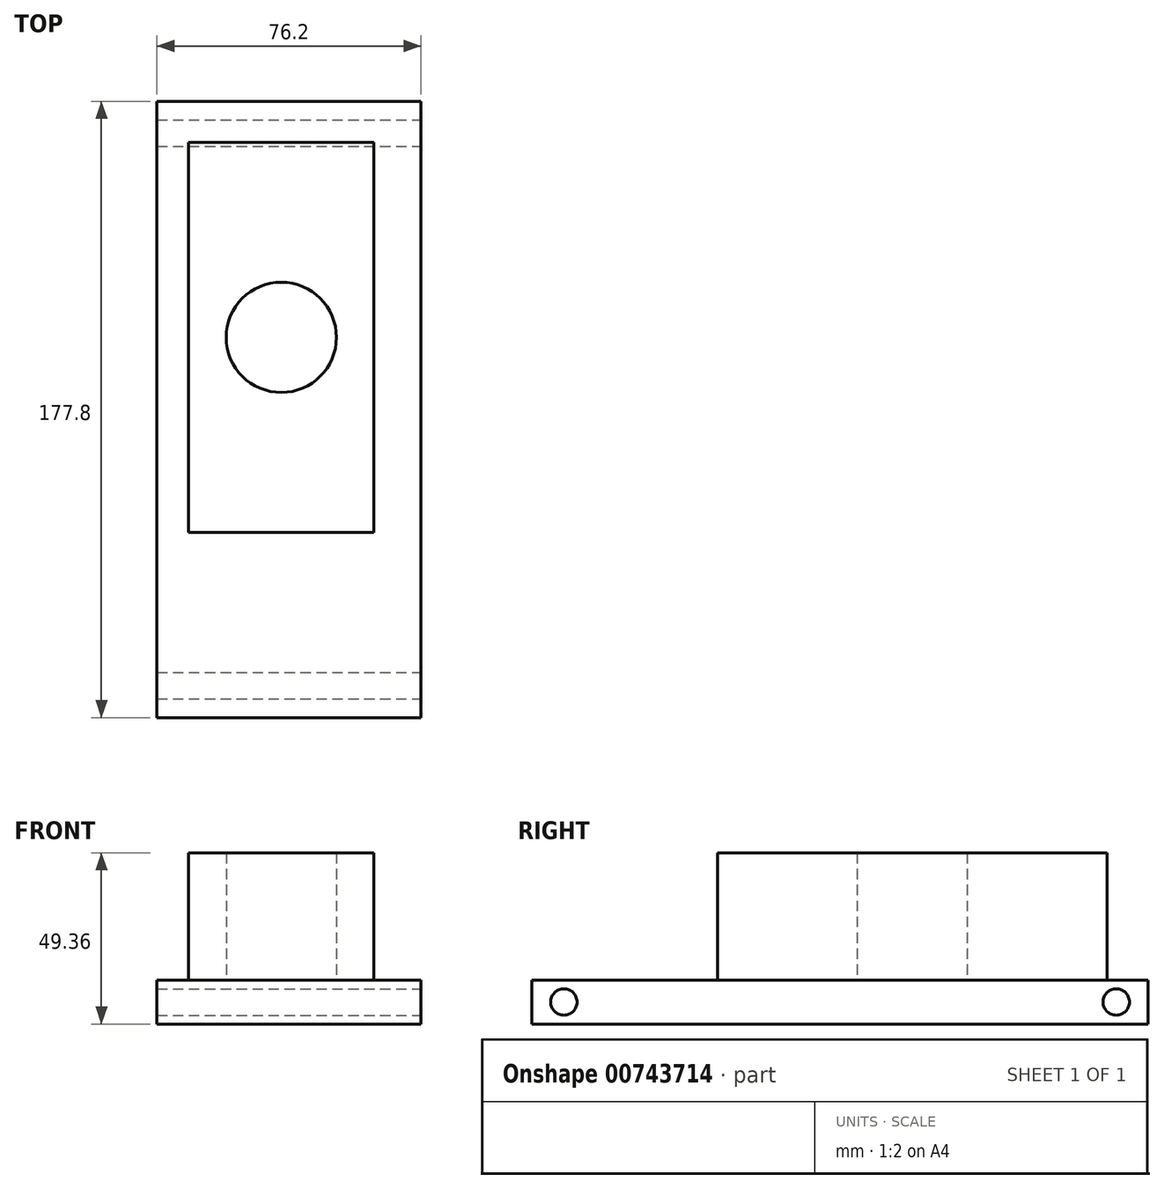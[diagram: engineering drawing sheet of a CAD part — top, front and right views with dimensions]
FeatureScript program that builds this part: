
annotation { "Feature Type Name" : "Feature", "Feature Type Description" : "" }
export const myFeature = defineFeature(function(context is Context, id is Id, definition is map)
    precondition{}
    {
        {
            var Q0;
            Q0=qCreatedBy(makeId("Top.planeOp"),FACE);
            var sketch = newSketch(context, id + "F0", { "sketchPlane" : qUnion([Q0])});
            skLineSegment(sketch, "E0.bottom", {"start": v(-49.4, 89.52) * mm, "end": v(26.8, 89.52) * mm});
            skLineSegment(sketch, "E0.top", {"start": v(-49.4, -88.28) * mm, "end": v(26.8, -88.28) * mm});
            skLineSegment(sketch, "E0.left", {"start": v(-49.4, 89.52) * mm, "end": v(-49.4, -88.28) * mm});
            skLineSegment(sketch, "E0.right", {"start": v(26.8, 89.52) * mm, "end": v(26.8, -88.28) * mm});
            skSolve(sketch);
        }
        {
            var Q0;
            Q0=makeQuery(id+"F0.imprint","IMPRINT",FACE,{"disambiguationData":[TD([[makeQuery(id+"F0.imprint","IMPRINT",EDGE,{"derivedFrom":sQuery(id+"F0.wireOp",EDGE,"E0.bottom")}),-1.0]])]});
            extrude(context, id + "F1", {"entities" : qUnion([Q0]), "depth" : 12.7 * mm, "offsetDistance" : 25.4 * mm});
        }
        {
            var Q0;
            Q0=makeQuery(id+"F1.opExtrude","SWEPT_FACE",FACE,{"disambiguationData":[OSD([sQuery(id+"F0.wireOp",EDGE,"E0.right")])]});
            var sketch = newSketch(context, id + "F2", { "sketchPlane" : qUnion([Q0])});
            skCircle(sketch, "E1", {"center": v(-79.06, 6.35) * mm, "radius": 3.81 * mm});
            skPoint(sketch, "E1.centerSnap0", {"position": v(-88.28, 6.35) * mm});
            skLineSegment(sketch, "E2", {"start": v(0.62, 12.7) * mm, "end": v(0.62, 0) * mm});
            skCircle(sketch, "E3.MirrorC", {"center": v(80.3, 6.35) * mm, "radius": 3.81 * mm});
            skSolve(sketch);
        }
        {
            var Q0;
            Q0=sQuery(id+"F2.wireOp",VERTEX,"E1.center");
            var Q1;
            Q1=makeQuery(id+"F1.opExtrude","SWEPT_BODY",BODY,{"disambiguationData":[OSD([sQuery(id+"F0.wireOp",EDGE,"E0.bottom"),sQuery(id+"F0.wireOp",EDGE,"E0.top"),sQuery(id+"F0.wireOp",EDGE,"E0.left"),sQuery(id+"F0.wireOp",EDGE,"E0.right")])]});
            hole(context, id + "F3", {"style" : HoleStyle.SIMPLE, "endStyle" : HoleEndStyle.THROUGH, "holeDiameter" : 7.62 * mm, "majorDiameter" : 6.35 * mm, "isTappedThrough" : true, "tappedDepth" : 12.7 * mm, "tapClearance" : 3, "locations" : qUnion([Q0]), "scope" : qUnion([Q1])});
        }
        {
            var Q0;
            Q0=sQuery(id+"F2.wireOp",VERTEX,"E3.MirrorC.center");
            var Q1;
            Q1=makeQuery(id+"F1.opExtrude","SWEPT_BODY",BODY,{"disambiguationData":[OSD([sQuery(id+"F0.wireOp",EDGE,"E0.bottom"),sQuery(id+"F0.wireOp",EDGE,"E0.top"),sQuery(id+"F0.wireOp",EDGE,"E0.left"),sQuery(id+"F0.wireOp",EDGE,"E0.right")])]});
            hole(context, id + "F4", {"style" : HoleStyle.SIMPLE, "endStyle" : HoleEndStyle.THROUGH, "holeDiameter" : 7.62 * mm, "majorDiameter" : 6.35 * mm, "isTappedThrough" : true, "tappedDepth" : 12.7 * mm, "tapClearance" : 3, "locations" : qUnion([Q0]), "scope" : qUnion([Q1])});
        }
        {
            var Q0;
            Q0=makeQuery(id+"F1.opExtrude","CAP_FACE",FACE,{"disambiguationData":[OSD([sQuery(id+"F0.wireOp",EDGE,"E0.bottom"),sQuery(id+"F0.wireOp",EDGE,"E0.top"),sQuery(id+"F0.wireOp",EDGE,"E0.left"),sQuery(id+"F0.wireOp",EDGE,"E0.right")])],"isStart":false});
            var sketch = newSketch(context, id + "F5", { "sketchPlane" : qUnion([Q0])});
            skSolve(sketch);
        }
        {
            var Q0;
            Q0=makeQuery(id+"F5.imprint","IMPRINT",FACE,{"disambiguationData":[TD([[makeQuery(id+"F5.imprint","IMPRINT",EDGE,{"derivedFrom":makeQuery(id+"F1.opExtrude","CAP_EDGE",EDGE,{"disambiguationData":[OSD([sQuery(id+"F0.wireOp",EDGE,"E0.bottom")])],"isStart":false})}),-1.0]])]});
            var sketch = newSketch(context, id + "F6", { "sketchPlane" : qUnion([Q0])});
            skLineSegment(sketch, "E4.bottom", {"start": v(13.2, -34.77) * mm, "end": v(-40.24, -34.77) * mm});
            skLineSegment(sketch, "E4.top", {"start": v(13.2, 77.66) * mm, "end": v(-40.24, 77.66) * mm});
            skLineSegment(sketch, "E4.left", {"start": v(13.2, -34.77) * mm, "end": v(13.2, 77.66) * mm});
            skLineSegment(sketch, "E4.right", {"start": v(-40.24, -34.77) * mm, "end": v(-40.24, 77.66) * mm});
            skPoint(sketch, "E4.middle", {"position": v(-13.52, 21.44) * mm});
            skCircle(sketch, "E5", {"center": v(-13.52, 21.44) * mm, "radius": 15.9 * mm});
            skSolve(sketch);
        }
        {
            var Q0;
            Q0=makeQuery(id+"F6.imprint","IMPRINT",FACE,{"disambiguationData":[TD([[makeQuery(id+"F6.imprint","IMPRINT",EDGE,{"derivedFrom":sQuery(id+"F6.wireOp",EDGE,"E4.bottom")}),-1.0]])]});
            extrude(context, id + "F7", {"entities" : qUnion([Q0]), "operationType" : NewBodyOperationType.ADD, "depth" : 36.66 * mm, "offsetDistance" : 25.4 * mm});
        }
    });
